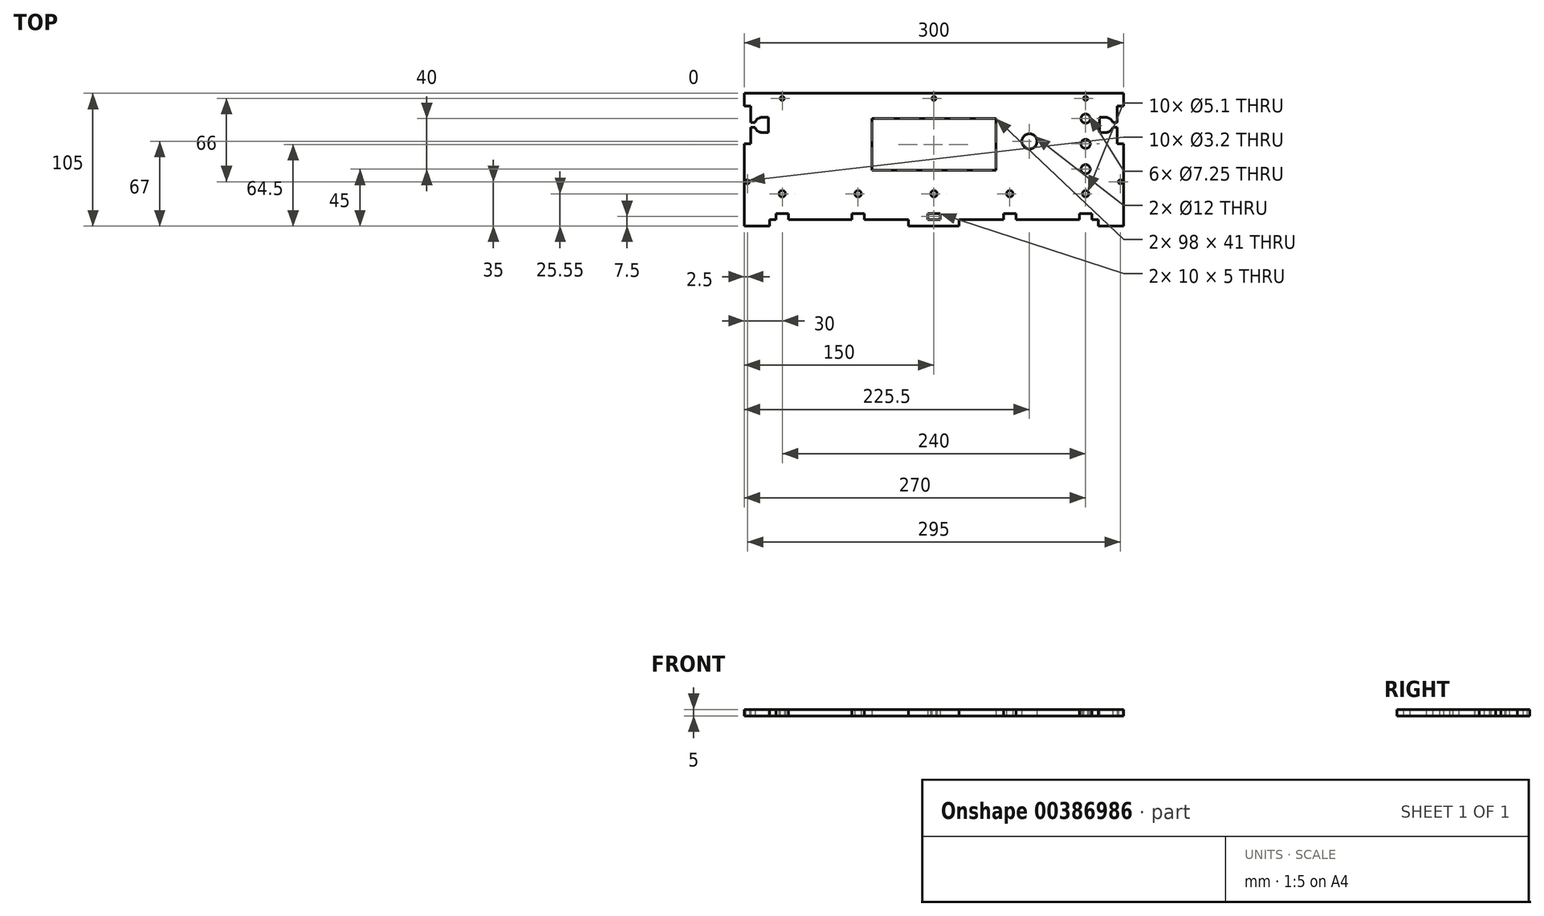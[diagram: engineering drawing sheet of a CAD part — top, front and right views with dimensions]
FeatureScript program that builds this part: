
annotation { "Feature Type Name" : "Feature", "Feature Type Description" : "" }
export const myFeature = defineFeature(function(context is Context, id is Id, definition is map)
    precondition{}
    {
        {
            var Q0;
            Q0=qCreatedBy(makeId("Top.planeOp"),FACE);
            var sketch = newSketch(context, id + "F0", { "sketchPlane" : qUnion([Q0])});
            skLineSegment(sketch, "E0.bottom", {"start": v(0, 0) * mm, "end": v(300, 0) * mm});
            skLineSegment(sketch, "E0.top", {"start": v(20, -100) * mm, "end": v(25, -100) * mm});
            skLineSegment(sketch, "E0.right", {"start": v(300, 0) * mm, "end": v(300, -10) * mm});
            skLineSegment(sketch, "E1.bottom", {"start": v(101, -20) * mm, "end": v(199, -20) * mm});
            skLineSegment(sketch, "E1.top", {"start": v(101, -61) * mm, "end": v(199, -61) * mm});
            skLineSegment(sketch, "E1.left", {"start": v(101, -20) * mm, "end": v(101, -61) * mm});
            skLineSegment(sketch, "E1.right", {"start": v(199, -20) * mm, "end": v(199, -61) * mm});
            skCircle(sketch, "E2", {"center": v(225.5, -38) * mm, "radius": 6 * mm});
            skCircle(sketch, "E3", {"center": v(30, -79.45) * mm, "radius": 2.55 * mm});
            skCircle(sketch, "E4", {"center": v(90, -79.45) * mm, "radius": 2.55 * mm});
            skCircle(sketch, "E5", {"center": v(150, -79.45) * mm, "radius": 2.55 * mm});
            skCircle(sketch, "E6", {"center": v(210, -79.45) * mm, "radius": 2.55 * mm});
            skCircle(sketch, "E7", {"center": v(270, -79.45) * mm, "radius": 2.55 * mm});
            skLineSegment(sketch, "E8.top", {"start": v(25, -95) * mm, "end": v(35, -95) * mm});
            skLineSegment(sketch, "E8.left", {"start": v(25, -100) * mm, "end": v(25, -95) * mm});
            skLineSegment(sketch, "E8.right", {"start": v(35, -100) * mm, "end": v(35, -95) * mm});
            skLineSegment(sketch, "E9.bottom", {"start": v(85, -95) * mm, "end": v(95, -95) * mm});
            skLineSegment(sketch, "E9.left", {"start": v(85, -95) * mm, "end": v(85, -100) * mm});
            skLineSegment(sketch, "E9.right", {"start": v(95, -95) * mm, "end": v(95, -100) * mm});
            skLineSegment(sketch, "E10.bottom", {"start": v(145, -95) * mm, "end": v(155, -95) * mm});
            skLineSegment(sketch, "E10.left", {"start": v(145, -95) * mm, "end": v(145, -100) * mm});
            skLineSegment(sketch, "E10.right", {"start": v(155, -95) * mm, "end": v(155, -100) * mm});
            skLineSegment(sketch, "E11.bottom", {"start": v(205, -95) * mm, "end": v(215, -95) * mm});
            skLineSegment(sketch, "E11.left", {"start": v(205, -95) * mm, "end": v(205, -100) * mm});
            skLineSegment(sketch, "E11.right", {"start": v(215, -95) * mm, "end": v(215, -100) * mm});
            skLineSegment(sketch, "E12.bottom", {"start": v(265, -95) * mm, "end": v(275, -95) * mm});
            skLineSegment(sketch, "E12.left", {"start": v(265, -95) * mm, "end": v(265, -100) * mm});
            skLineSegment(sketch, "E12.right", {"start": v(275, -95) * mm, "end": v(275, -100) * mm});
            skLineSegment(sketch, "E13.top", {"start": v(0, -105) * mm, "end": v(20, -105) * mm});
            skLineSegment(sketch, "E13.left", {"start": v(0, -100) * mm, "end": v(0, -105) * mm});
            skLineSegment(sketch, "E13.right", {"start": v(20, -100) * mm, "end": v(20, -105) * mm});
            skLineSegment(sketch, "E14.trimOffspring", {"start": v(35, -100) * mm, "end": v(85, -100) * mm});
            skLineSegment(sketch, "E15.trimOffspring", {"start": v(95, -100) * mm, "end": v(130, -100) * mm});
            skLineSegment(sketch, "E16.trimOffspring", {"start": v(170, -100) * mm, "end": v(205, -100) * mm});
            skLineSegment(sketch, "E17.trimOffspring", {"start": v(215, -100) * mm, "end": v(265, -100) * mm});
            skLineSegment(sketch, "E18.trimOffspring", {"start": v(275, -100) * mm, "end": v(280, -100) * mm});
            skLineSegment(sketch, "E19.top", {"start": v(300, -105) * mm, "end": v(280, -105) * mm});
            skLineSegment(sketch, "E19.left", {"start": v(300, -100) * mm, "end": v(300, -105) * mm});
            skLineSegment(sketch, "E19.right", {"start": v(280, -100) * mm, "end": v(280, -105) * mm});
            skLineSegment(sketch, "E20.bottom", {"start": v(145, -100) * mm, "end": v(155, -100) * mm});
            skLineSegment(sketch, "E20.top", {"start": v(130, -105) * mm, "end": v(170, -105) * mm});
            skLineSegment(sketch, "E20.left", {"start": v(130, -100) * mm, "end": v(130, -105) * mm});
            skLineSegment(sketch, "E20.right", {"start": v(170, -100) * mm, "end": v(170, -105) * mm});
            skCircle(sketch, "E21", {"center": v(270, -20) * mm, "radius": 3.62 * mm});
            skCircle(sketch, "E22", {"center": v(270, -40) * mm, "radius": 3.62 * mm});
            skLineSegment(sketch, "E23", {"start": v(19.16, -19) * mm, "end": v(19.16, -31) * mm});
            skLineSegment(sketch, "E24", {"start": v(19.16, -19) * mm, "end": v(14.16, -19) * mm});
            skLineSegment(sketch, "E25", {"start": v(19.16, -31) * mm, "end": v(14.16, -31) * mm});
            skLineSegment(sketch, "E26", {"start": v(5, -23) * mm, "end": v(8.5, -23) * mm});
            skLineSegment(sketch, "E27", {"start": v(5, -27) * mm, "end": v(8.5, -27) * mm});
            skArc(sketch, "E28", {"start": v(14.16, -19) * mm, "mid": v(10.7, -20.1) * mm, "end": v(8.5, -23) * mm});
            skArc(sketch, "E29.trimOffspring", {"start": v(8.5, -27) * mm, "mid": v(10.7, -29.9) * mm, "end": v(14.16, -31) * mm});
            skLineSegment(sketch, "E30", {"start": v(0, 0) * mm, "end": v(0, -10) * mm});
            skLineSegment(sketch, "E31.bottom", {"start": v(0, -10) * mm, "end": v(5, -10) * mm});
            skLineSegment(sketch, "E31.top", {"start": v(0, -40) * mm, "end": v(5, -40) * mm});
            skLineSegment(sketch, "E31.right", {"start": v(5, -10) * mm, "end": v(5, -23) * mm});
            skLineSegment(sketch, "E32.trimOffspring", {"start": v(5, -27) * mm, "end": v(5, -40) * mm});
            skLineSegment(sketch, "E33.trimOffspring", {"start": v(0, -40) * mm, "end": v(0, -100) * mm});
            skCircle(sketch, "E34", {"center": v(2.5, -70) * mm, "radius": 1.6 * mm});
            skLineSegment(sketch, "E35", {"start": v(280.84, -31) * mm, "end": v(280.84, -19) * mm});
            skLineSegment(sketch, "E36", {"start": v(280.84, -31) * mm, "end": v(285.84, -31) * mm});
            skLineSegment(sketch, "E37", {"start": v(280.84, -19) * mm, "end": v(285.84, -19) * mm});
            skLineSegment(sketch, "E38", {"start": v(295, -27) * mm, "end": v(291.5, -27) * mm});
            skLineSegment(sketch, "E39", {"start": v(295, -23) * mm, "end": v(291.5, -23) * mm});
            skArc(sketch, "E40", {"start": v(285.84, -31) * mm, "mid": v(289.3, -29.9) * mm, "end": v(291.5, -27) * mm});
            skArc(sketch, "E41.trimOffspring", {"start": v(291.5, -23) * mm, "mid": v(289.3, -20.1) * mm, "end": v(285.84, -19) * mm});
            skLineSegment(sketch, "E42.bottom", {"start": v(300, -40) * mm, "end": v(295, -40) * mm});
            skLineSegment(sketch, "E42.top", {"start": v(300, -10) * mm, "end": v(295, -10) * mm});
            skLineSegment(sketch, "E42.right", {"start": v(295, -40) * mm, "end": v(295, -27) * mm});
            skLineSegment(sketch, "E43.trimOffspring", {"start": v(295, -23) * mm, "end": v(295, -10) * mm});
            skCircle(sketch, "E44", {"center": v(297.5, -70) * mm, "radius": 1.6 * mm});
            skLineSegment(sketch, "E45.trimOffspring", {"start": v(300, -40) * mm, "end": v(300, -100) * mm});
            skCircle(sketch, "E46", {"center": v(30, -4) * mm, "radius": 1.6 * mm});
            skCircle(sketch, "E47", {"center": v(150, -4) * mm, "radius": 1.6 * mm});
            skCircle(sketch, "E48", {"center": v(270, -4) * mm, "radius": 1.6 * mm});
            skCircle(sketch, "E49", {"center": v(270, -60) * mm, "radius": 3.62 * mm});
            skSolve(sketch);
        }
        {
            var Q0;
            Q0=makeQuery(id+"F0.imprint","IMPRINT",FACE,{"disambiguationData":[TD([[makeQuery(id+"F0.imprint","IMPRINT",EDGE,{"derivedFrom":sQuery(id+"F0.wireOp",EDGE,"E0.bottom")}),-1.0]])]});
            extrude(context, id + "F1", {"entities" : qUnion([Q0]), "depth" : 5 * mm});
        }
    });
